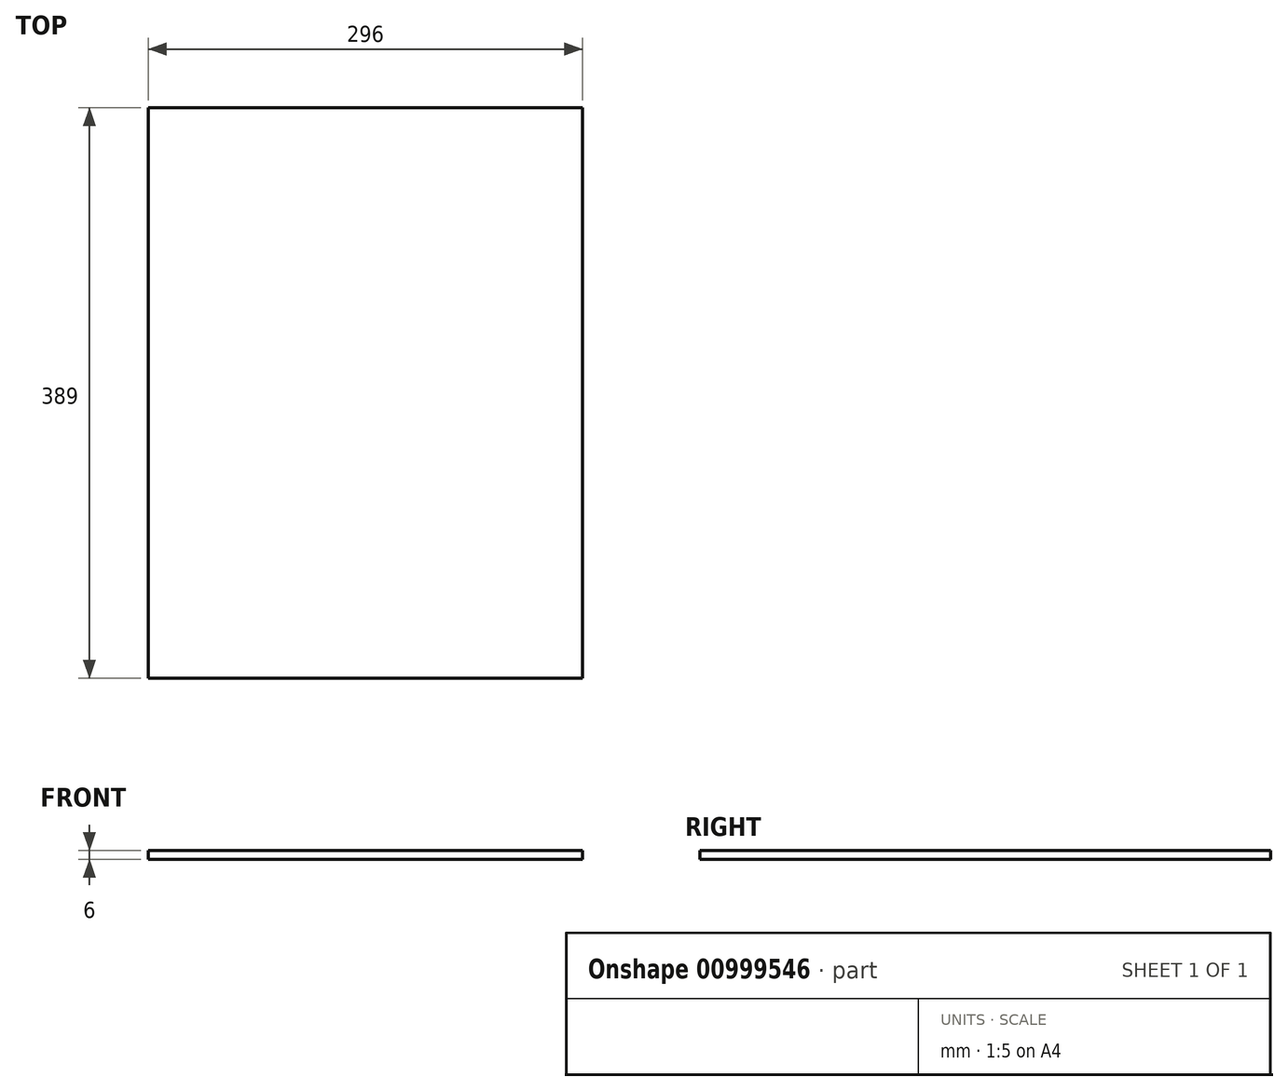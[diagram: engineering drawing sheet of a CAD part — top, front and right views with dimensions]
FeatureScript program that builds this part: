
annotation { "Feature Type Name" : "Feature", "Feature Type Description" : "" }
export const myFeature = defineFeature(function(context is Context, id is Id, definition is map)
    precondition{}
    {
        {
            var Q0;
            Q0=qCreatedBy(makeId("Top.planeOp"),FACE);
            var sketch = newSketch(context, id + "F0", { "sketchPlane" : qUnion([Q0]), "disableImprinting" : false});
            skLineSegment(sketch, "E0.bottom", {"start": v(-148, 194.5) * mm, "end": v(148, 194.5) * mm});
            skLineSegment(sketch, "E0.top", {"start": v(-148, -194.5) * mm, "end": v(148, -194.5) * mm});
            skLineSegment(sketch, "E0.left", {"start": v(-148, 194.5) * mm, "end": v(-148, -194.5) * mm});
            skLineSegment(sketch, "E0.right", {"start": v(148, 194.5) * mm, "end": v(148, -194.5) * mm});
            skPoint(sketch, "E0.middle", {"position": v(0, 0) * mm});
            skSolve(sketch);
        }
        {
            var Q0;
            Q0=makeQuery(id+"F0.imprint","IMPRINT",FACE,{"disambiguationData":[TD([[makeQuery(id+"F0.imprint","IMPRINT",EDGE,{"derivedFrom":sQuery(id+"F0.wireOp",EDGE,"E0.bottom")}),-1.0]])]});
            extrude(context, id + "F1", {"entities" : qUnion([Q0]), "flatOperationType" : FlatOperationType.REMOVE, "thickness1" : 5 * mm, "thickness2" : 0 * mm, "thickness" : 5 * mm, "depth" : 6 * mm, "offsetDistance" : 25 * mm, "startOffsetBound" : StartOffsetType.BLIND, "startOffsetDistance" : 25 * mm, "domain" : OperationDomain.MODEL});
        }
    });
